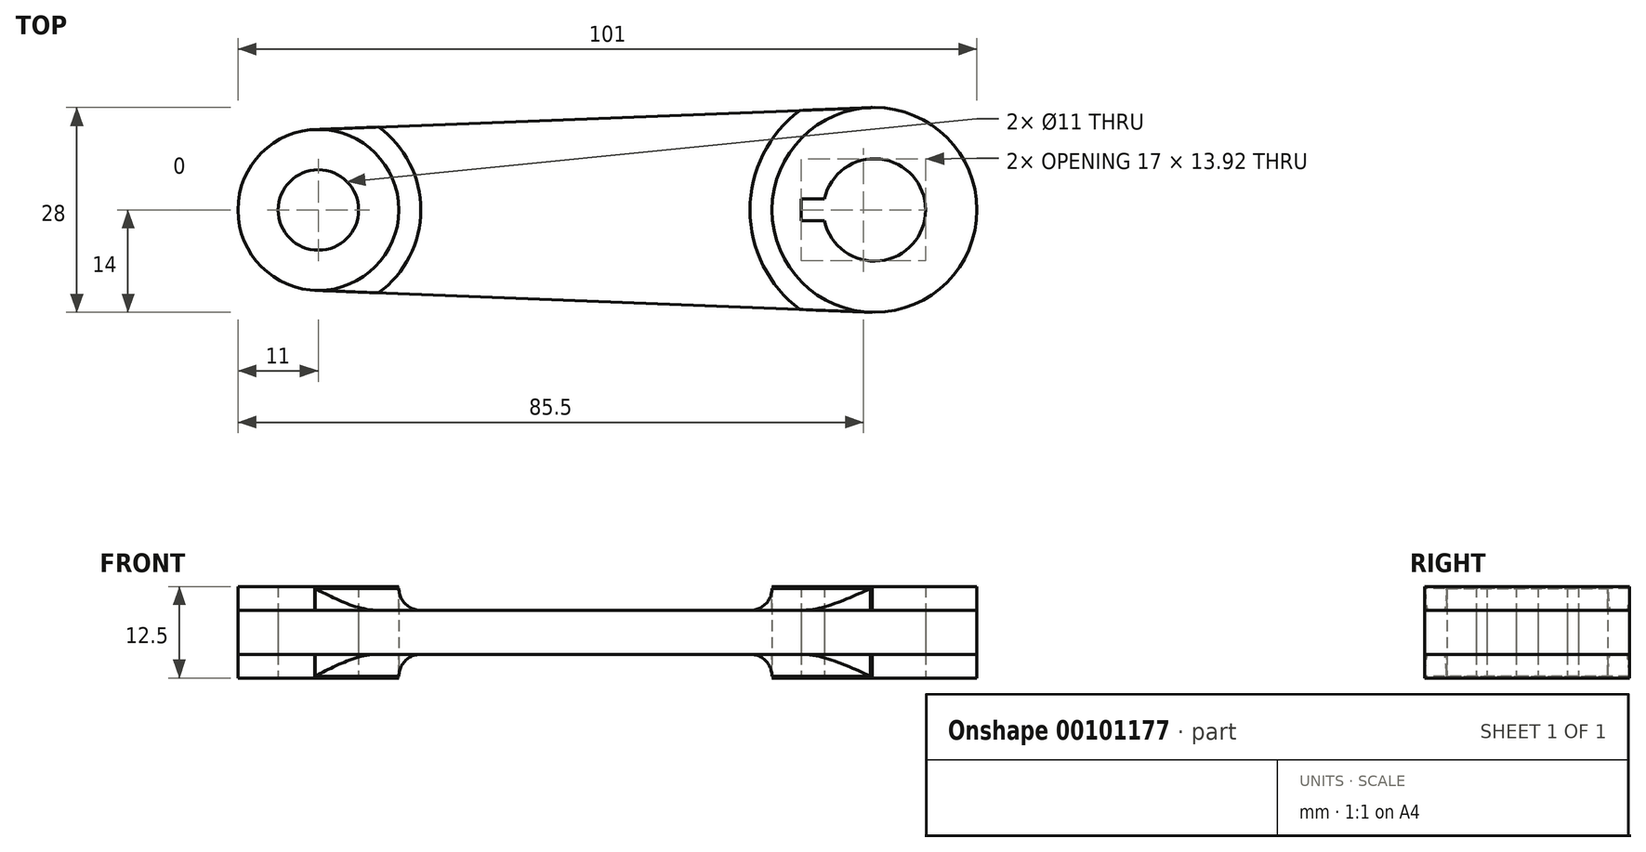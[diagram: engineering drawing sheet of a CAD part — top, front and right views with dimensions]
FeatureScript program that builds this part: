
annotation { "Feature Type Name" : "Feature", "Feature Type Description" : "" }
export const myFeature = defineFeature(function(context is Context, id is Id, definition is map)
    precondition{}
    {
        {
            var Q0;
            Q0=qCreatedBy(makeId("Top.planeOp"),FACE);
            var sketch = newSketch(context, id + "F0", { "sketchPlane" : qUnion([Q0])});
            skArc(sketch, "E0", {"start": v(-6.84, -1.5) * mm, "mid": v(7, 0) * mm, "end": v(-6.84, 1.5) * mm});
            skCircle(sketch, "E1", {"center": v(0, 0) * mm, "radius": 14 * mm});
            skCircle(sketch, "E2", {"center": v(-76, 0) * mm, "radius": 5.5 * mm});
            skCircle(sketch, "E3", {"center": v(-76, 0) * mm, "radius": 11 * mm});
            skLineSegment(sketch, "E4", {"start": v(-76.43, 11) * mm, "end": v(0, 14.01) * mm});
            skLineSegment(sketch, "E5", {"start": v(-76.43, -11) * mm, "end": v(-0.55, -13.99) * mm});
            skLineSegment(sketch, "E6", {"start": v(-10, 1.5) * mm, "end": v(-10, -1.5) * mm});
            skLineSegment(sketch, "E7", {"start": v(-10, 1.5) * mm, "end": v(-6.84, 1.5) * mm});
            skLineSegment(sketch, "E8", {"start": v(-10, -1.5) * mm, "end": v(-6.84, -1.5) * mm});
            skLineSegment(sketch, "E9", {"start": v(-76.43, -11) * mm, "end": v(0, -11) * mm, "construction": true});
            skSolve(sketch);
        }
        {
            var Q0;
            Q0=makeQuery(id+"F0.imprint","IMPRINT",FACE,{"disambiguationData":[TD([[makeQuery(id+"F0.imprint","IMPRINT",EDGE,{"derivedFrom":sQuery(id+"F0.wireOp",EDGE,"E2")}),-1.0]])]});
            var Q1;
            Q1=makeQuery(id+"F0.imprint","IMPRINT",FACE,{"disambiguationData":[TD([[makeQuery(id+"F0.imprint","IMPRINT",EDGE,{"derivedFrom":sQuery(id+"F0.wireOp",EDGE,"E0")}),-1.0]])]});
            extrude(context, id + "F1", {"entities" : qUnion([Q0, Q1]), "endBound" : BoundingType.SYMMETRIC, "depth" : 12.5 * mm});
        }
        {
            var Q0;
            Q0=qSketchRegion(id+"F0",true);
            extrude(context, id + "F2", {"entities" : qUnion([Q0]), "endBound" : BoundingType.SYMMETRIC, "depth" : 6 * mm});
        }
        {
            var Q0;
            Q0=qCreatedBy(makeId("Front.planeOp"),FACE);
            var sketch = newSketch(context, id + "F3", { "sketchPlane" : qUnion([Q0])});
            skArc(sketch, "E10", {"start": v(-65, 6) * mm, "mid": v(-64.12, 3.88) * mm, "end": v(-62, 3) * mm});
            skLineSegment(sketch, "E11", {"start": v(-65, 3) * mm, "end": v(-65, 9.2) * mm, "construction": true});
            skLineSegment(sketch, "E12", {"start": v(-65, 3) * mm, "end": v(-52.33, 3) * mm, "construction": true});
            skLineSegment(sketch, "E13", {"start": v(-65, 6) * mm, "end": v(-65, 3) * mm});
            skLineSegment(sketch, "E14", {"start": v(-62, 3) * mm, "end": v(-65, 3) * mm});
            skLineSegment(sketch, "E15", {"start": v(-76, 24.5) * mm, "end": v(-76, -22.06) * mm, "construction": true});
            skLineSegment(sketch, "E16.MirrorCS", {"start": v(-62, -3) * mm, "end": v(-65, -3) * mm});
            skLineSegment(sketch, "E17.MirrorCS", {"start": v(-65, -6) * mm, "end": v(-65, -3) * mm});
            skArc(sketch, "E18.MirrorCS", {"start": v(-65, -6) * mm, "mid": v(-64.12, -3.88) * mm, "end": v(-62, -3) * mm});
            skLineSegment(sketch, "E19", {"start": v(-14, 3) * mm, "end": v(-14, 6) * mm});
            skLineSegment(sketch, "E20", {"start": v(-14, 3) * mm, "end": v(-17, 3) * mm});
            skArc(sketch, "E21", {"start": v(-14, 6) * mm, "mid": v(-14.88, 3.88) * mm, "end": v(-17, 3) * mm});
            skLineSegment(sketch, "E22.MirrorCS", {"start": v(-14, -3) * mm, "end": v(-14, -6) * mm});
            skLineSegment(sketch, "E23.MirrorCS", {"start": v(-14, -3) * mm, "end": v(-17, -3) * mm});
            skArc(sketch, "E24.MirrorCS", {"start": v(-14, -6) * mm, "mid": v(-14.88, -3.88) * mm, "end": v(-17, -3) * mm});
            skLineSegment(sketch, "E25", {"start": v(0, 40.72) * mm, "end": v(0, -63.9) * mm, "construction": true});
            skSolve(sketch);
        }
        {
            var Q0;
            Q0=makeQuery(id+"F3.imprint","IMPRINT",FACE,{"disambiguationData":[TD([[makeQuery(id+"F3.imprint","IMPRINT",EDGE,{"derivedFrom":sQuery(id+"F3.wireOp",EDGE,"E10")}),-1.0]])]});
            var Q1;
            Q1=makeQuery(id+"F3.imprint","IMPRINT",FACE,{"disambiguationData":[TD([[makeQuery(id+"F3.imprint","IMPRINT",EDGE,{"derivedFrom":sQuery(id+"F3.wireOp",EDGE,"E16.MirrorCS")}),1.0]])]});
            var Q2;
            Q2=sQuery(id+"F3.wireOp",EDGE,"E15");
            revolve(context, id + "F4", {"entities" : qUnion([Q0, Q1]), "axis" : qUnion([Q2]), "revolveType" : RevolveType.SYMMETRIC, "angle" : 185 * degree});
        }
        {
            var Q0;
            Q0=makeQuery(id+"F3.imprint","IMPRINT",FACE,{"disambiguationData":[TD([[makeQuery(id+"F3.imprint","IMPRINT",EDGE,{"derivedFrom":sQuery(id+"F3.wireOp",EDGE,"E19")}),1.0]])]});
            var Q1;
            Q1=makeQuery(id+"F3.imprint","IMPRINT",FACE,{"disambiguationData":[TD([[makeQuery(id+"F3.imprint","IMPRINT",EDGE,{"derivedFrom":sQuery(id+"F3.wireOp",EDGE,"E22.MirrorCS")}),-1.0]])]});
            var Q2;
            Q2=sQuery(id+"F3.wireOp",EDGE,"E25");
            revolve(context, id + "F5", {"entities" : qUnion([Q0, Q1]), "axis" : qUnion([Q2]), "revolveType" : RevolveType.SYMMETRIC, "angle" : 177.74 * degree});
        }
        {
            var Q0;
            Q0=qCreatedBy(makeId("Top.planeOp"),FACE);
            var sketch = newSketch(context, id + "F6", { "sketchPlane" : qUnion([Q0])});
            skLineSegment(sketch, "E26", {"start": v(-90.89, -10.42) * mm, "end": v(10.3, -14.42) * mm});
            skLineSegment(sketch, "E27", {"start": v(-90.89, -10.42) * mm, "end": v(-91.18, -17.9) * mm});
            skLineSegment(sketch, "E28", {"start": v(-91.18, -17.9) * mm, "end": v(10, -21.9) * mm});
            skLineSegment(sketch, "E29", {"start": v(10, -21.9) * mm, "end": v(10.3, -14.42) * mm});
            skLineSegment(sketch, "E30.MirrorCS", {"start": v(-90.89, 10.42) * mm, "end": v(-91.18, 17.9) * mm});
            skLineSegment(sketch, "E31.MirrorCS", {"start": v(10, 21.9) * mm, "end": v(10.3, 14.42) * mm});
            skLineSegment(sketch, "E32.MirrorCS", {"start": v(-90.89, 10.42) * mm, "end": v(10.3, 14.42) * mm});
            skLineSegment(sketch, "E33.MirrorCS", {"start": v(-91.18, 17.9) * mm, "end": v(10, 21.9) * mm});
            skSolve(sketch);
        }
        {
            var Q0;
            Q0=makeQuery(id+"F6.imprint","IMPRINT",FACE,{"disambiguationData":[TD([[makeQuery(id+"F6.imprint","IMPRINT",EDGE,{"derivedFrom":sQuery(id+"F6.wireOp",EDGE,"E30.MirrorCS")}),-1.0]])]});
            var Q1;
            Q1=makeQuery(id+"F6.imprint","IMPRINT",FACE,{"disambiguationData":[TD([[makeQuery(id+"F6.imprint","IMPRINT",EDGE,{"derivedFrom":sQuery(id+"F6.wireOp",EDGE,"E26")}),-1.0]])]});
            extrude(context, id + "F7", {"entities" : qUnion([Q0, Q1]), "operationType" : NewBodyOperationType.REMOVE, "endBound" : BoundingType.SYMMETRIC, "oppositeDirection" : true, "depth" : 25 * mm});
        }
    });
